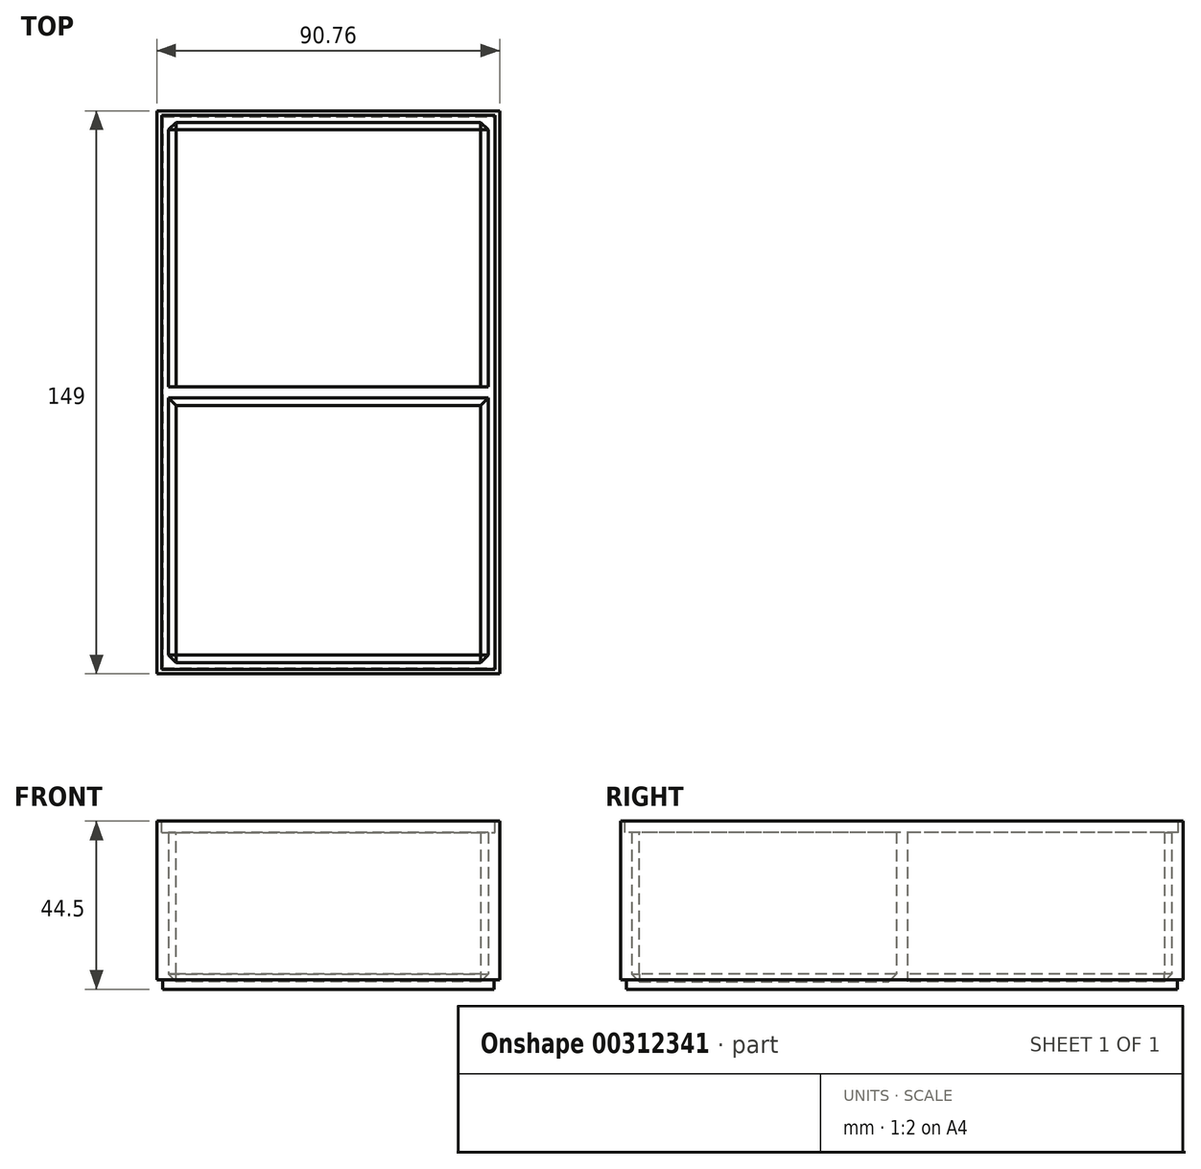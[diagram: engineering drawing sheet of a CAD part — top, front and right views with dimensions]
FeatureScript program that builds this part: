
annotation { "Feature Type Name" : "Feature", "Feature Type Description" : "" }
export const myFeature = defineFeature(function(context is Context, id is Id, definition is map)
    precondition{}
    {
        {
            assignVariable(context, id + "F0", {"name" : "BoxHeight", "anyValue" : 44.5 * mm});
        }
        {
            var Q0;
            Q0=qCreatedBy(makeId("Top.planeOp"),FACE);
            var sketch = newSketch(context, id + "F1", { "sketchPlane" : qUnion([Q0])});
            skLineSegment(sketch, "E0.bottom", {"start": v(-45.37, 74.5) * mm, "end": v(45.38, 74.5) * mm});
            skLineSegment(sketch, "E0.top", {"start": v(-45.38, -74.5) * mm, "end": v(45.37, -74.5) * mm});
            skLineSegment(sketch, "E0.left", {"start": v(-45.37, 74.5) * mm, "end": v(-45.38, -74.5) * mm});
            skLineSegment(sketch, "E0.right", {"start": v(45.38, 74.5) * mm, "end": v(45.37, -74.5) * mm});
            skPoint(sketch, "E0.middle", {"position": v(0, 0) * mm});
            skLineSegment(sketch, "E1.0", {"start": v(-42.37, 71.5) * mm, "end": v(42.38, 71.5) * mm});
            skLineSegment(sketch, "E1.1", {"start": v(-42.37, 71.5) * mm, "end": v(-42.38, -71.5) * mm});
            skLineSegment(sketch, "E1.2", {"start": v(-42.38, -71.5) * mm, "end": v(42.37, -71.5) * mm});
            skLineSegment(sketch, "E1.3", {"start": v(42.38, 71.5) * mm, "end": v(42.37, -71.5) * mm});
            skSolve(sketch);
        }
        {
            var Q0;
            Q0=makeQuery(id+"F1.imprint","IMPRINT",FACE,{"disambiguationData":[TD([[makeQuery(id+"F1.imprint","IMPRINT",EDGE,{"derivedFrom":sQuery(id+"F1.wireOp",EDGE,"E0.bottom")}),-1.0]])]});
            extrude(context, id + "F2", {"entities" : qUnion([Q0]), "depth" : getVariable(context, 'BoxHeight')});
        }
        {
            var Q0;
            Q0=qSketchRegion(id+"F1",true);
            var Q1;
            Q1=makeQuery(id+"F1.imprint","IMPRINT",FACE,{"disambiguationData":[TD([[makeQuery(id+"F1.imprint","IMPRINT",EDGE,{"derivedFrom":sQuery(id+"F1.wireOp",EDGE,"E1.0")}),-1.0]])]});
            extrude(context, id + "F3", {"entities" : qUnion([Q0, Q1]), "operationType" : NewBodyOperationType.ADD, "depth" : 2 * mm});
        }
        {
            var Q0;
            Q0=makeQuery(id+"F2.opExtrude","CAP_FACE",FACE,{"disambiguationData":[OSD([sQuery(id+"F1.wireOp",EDGE,"E0.bottom"),sQuery(id+"F1.wireOp",EDGE,"E0.top"),sQuery(id+"F1.wireOp",EDGE,"E0.left"),sQuery(id+"F1.wireOp",EDGE,"E0.right"),sQuery(id+"F1.wireOp",EDGE,"E1.0"),sQuery(id+"F1.wireOp",EDGE,"E1.1"),sQuery(id+"F1.wireOp",EDGE,"E1.2"),sQuery(id+"F1.wireOp",EDGE,"E1.3")])],"isStart":false});
            var sketch = newSketch(context, id + "F4", { "sketchPlane" : qUnion([Q0])});
            skLineSegment(sketch, "E2.0", {"start": v(-45.37, 74.5) * mm, "end": v(45.38, 74.5) * mm});
            skLineSegment(sketch, "E2.1", {"start": v(45.38, 74.5) * mm, "end": v(45.37, -74.5) * mm});
            skLineSegment(sketch, "E2.2", {"start": v(-45.37, 74.5) * mm, "end": v(-45.38, -74.5) * mm});
            skLineSegment(sketch, "E2.3", {"start": v(-45.38, -74.5) * mm, "end": v(45.37, -74.5) * mm});
            skLineSegment(sketch, "E3.0", {"start": v(-44.17, 73.3) * mm, "end": v(-44.18, -73.3) * mm});
            skLineSegment(sketch, "E3.1", {"start": v(-44.17, 73.3) * mm, "end": v(44.17, 73.3) * mm});
            skLineSegment(sketch, "E3.2", {"start": v(44.18, 73.3) * mm, "end": v(44.17, -73.3) * mm});
            skLineSegment(sketch, "E3.3", {"start": v(-44.18, -73.3) * mm, "end": v(44.17, -73.3) * mm});
            skSolve(sketch);
        }
        {
            var Q0;
            Q0=makeQuery(id+"F4.imprint","IMPRINT",FACE,{"disambiguationData":[TD([[makeQuery(id+"F4.imprint","IMPRINT",EDGE,{"derivedFrom":sQuery(id+"F4.wireOp",EDGE,"E3.0")}),1.0]])]});
            extrude(context, id + "F5", {"entities" : qUnion([Q0]), "operationType" : NewBodyOperationType.REMOVE, "oppositeDirection" : true, "depth" : 3 * mm});
        }
        {
            var Q0;
            {var subQ0=sQuery(id+"F1.wireOp",EDGE,"E0.right");var subQ1=sQuery(id+"F1.wireOp",EDGE,"E0.left");var subQ2=sQuery(id+"F1.wireOp",EDGE,"E0.top");var subQ3=sQuery(id+"F1.wireOp",EDGE,"E0.bottom");Q0=makeQuery(id+"F3.boolean.opBoolean","MERGE",FACE,{"derivedFrom":[makeQuery(id+"F2.opExtrude","CAP_FACE",FACE,{"disambiguationData":[OSD([subQ3,subQ2,subQ1,subQ0,sQuery(id+"F1.wireOp",EDGE,"E1.0"),sQuery(id+"F1.wireOp",EDGE,"E1.1"),sQuery(id+"F1.wireOp",EDGE,"E1.2"),sQuery(id+"F1.wireOp",EDGE,"E1.3")])],"isStart":true}),makeQuery(id+"F3.opExtrude","CAP_FACE",FACE,{"disambiguationData":[OSD([subQ3,subQ2,subQ1,subQ0])],"isStart":true})]});}
            var sketch = newSketch(context, id + "F6", { "sketchPlane" : qUnion([Q0])});
            skLineSegment(sketch, "E4.0", {"start": v(-45.37, -74.5) * mm, "end": v(-45.38, 74.5) * mm});
            skLineSegment(sketch, "E5.0", {"start": v(-45.38, 74.5) * mm, "end": v(45.37, 74.5) * mm});
            skLineSegment(sketch, "E6.0", {"start": v(45.38, -74.5) * mm, "end": v(45.37, 74.5) * mm});
            skLineSegment(sketch, "E7.0", {"start": v(-45.37, -74.5) * mm, "end": v(45.38, -74.5) * mm});
            skLineSegment(sketch, "E8.0", {"start": v(-43.87, -73) * mm, "end": v(-43.88, 73) * mm});
            skLineSegment(sketch, "E8.1", {"start": v(-43.87, -73) * mm, "end": v(43.88, -73) * mm});
            skLineSegment(sketch, "E8.2", {"start": v(43.88, -73) * mm, "end": v(43.87, 73) * mm});
            skLineSegment(sketch, "E8.3", {"start": v(-43.88, 73) * mm, "end": v(43.87, 73) * mm});
            skSolve(sketch);
        }
        {
            var Q0;
            Q0=makeQuery(id+"F6.imprint","IMPRINT",FACE,{"disambiguationData":[TD([[makeQuery(id+"F6.imprint","IMPRINT",EDGE,{"derivedFrom":sQuery(id+"F6.wireOp",EDGE,"E4.0")}),-1.0]])]});
            extrude(context, id + "F7", {"entities" : qUnion([Q0]), "operationType" : NewBodyOperationType.REMOVE, "oppositeDirection" : true, "depth" : 2.5 * mm});
        }
        {
            var Q0;
            Q0=makeQuery(id+"F2.opExtrude","SWEPT_FACE",FACE,{"disambiguationData":[OSD([sQuery(id+"F1.wireOp",EDGE,"E1.3")])]});
            var sketch = newSketch(context, id + "F8", { "sketchPlane" : qUnion([Q0])});
            skLineSegment(sketch, "E9", {"start": v(0, 41.5) * mm, "end": v(0, 2) * mm});
            skSolve(sketch);
        }
        {
            var Q0;
            Q0=sQuery(id+"F8.wireOp",EDGE,"E9");
            extrude(context, id + "F9", {"bodyType" : ToolBodyType.SURFACE, "surfaceEntities" : qUnion([Q0]), "endBound" : BoundingType.UP_TO_NEXT, "depth" : 25 * mm});
        }
        {
            var Q0;
            Q0=makeQuery(id+"F9.opExtrude","SWEPT_FACE",FACE,{"disambiguationData":[OSD([sQuery(id+"F8.wireOp",EDGE,"E9")])]});
            extrude(context, id + "F10", {"entities" : qUnion([Q0]), "operationType" : NewBodyOperationType.ADD, "endBound" : BoundingType.SYMMETRIC, "depth" : 3 * mm});
        }
        {
            var Q0;
            Q0=makeQuery(id+"F3.boolean.opBoolean","INTERSECT",EDGE,{"derivedFrom":[makeQuery(id+"F2.opExtrude","SWEPT_FACE",FACE,{"disambiguationData":[OSD([sQuery(id+"F1.wireOp",EDGE,"E1.0")])]}),makeQuery(id+"F3.opExtrude","CAP_FACE",FACE,{"disambiguationData":[OSD([sQuery(id+"F1.wireOp",EDGE,"E0.bottom"),sQuery(id+"F1.wireOp",EDGE,"E0.top"),sQuery(id+"F1.wireOp",EDGE,"E0.left"),sQuery(id+"F1.wireOp",EDGE,"E0.right")])],"isStart":false})]});
            var Q1;
            Q1=makeQuery(id+"F3.boolean.opBoolean","INTERSECT",EDGE,{"derivedFrom":[makeQuery(id+"F2.opExtrude","SWEPT_FACE",FACE,{"disambiguationData":[OSD([sQuery(id+"F1.wireOp",EDGE,"E1.3")])]}),makeQuery(id+"F3.opExtrude","CAP_FACE",FACE,{"disambiguationData":[OSD([sQuery(id+"F1.wireOp",EDGE,"E0.bottom"),sQuery(id+"F1.wireOp",EDGE,"E0.top"),sQuery(id+"F1.wireOp",EDGE,"E0.left"),sQuery(id+"F1.wireOp",EDGE,"E0.right")])],"isStart":false})]});
            var Q2;
            Q2=makeQuery(id+"F3.boolean.opBoolean","INTERSECT",EDGE,{"derivedFrom":[makeQuery(id+"F2.opExtrude","SWEPT_FACE",FACE,{"disambiguationData":[OSD([sQuery(id+"F1.wireOp",EDGE,"E1.1")])]}),makeQuery(id+"F3.opExtrude","CAP_FACE",FACE,{"disambiguationData":[OSD([sQuery(id+"F1.wireOp",EDGE,"E0.bottom"),sQuery(id+"F1.wireOp",EDGE,"E0.top"),sQuery(id+"F1.wireOp",EDGE,"E0.left"),sQuery(id+"F1.wireOp",EDGE,"E0.right")])],"isStart":false})]});
            var Q3;
            Q3=makeQuery(id+"F3.boolean.opBoolean","INTERSECT",EDGE,{"derivedFrom":[makeQuery(id+"F2.opExtrude","SWEPT_FACE",FACE,{"disambiguationData":[OSD([sQuery(id+"F1.wireOp",EDGE,"E1.2")])]}),makeQuery(id+"F3.opExtrude","CAP_FACE",FACE,{"disambiguationData":[OSD([sQuery(id+"F1.wireOp",EDGE,"E0.bottom"),sQuery(id+"F1.wireOp",EDGE,"E0.top"),sQuery(id+"F1.wireOp",EDGE,"E0.left"),sQuery(id+"F1.wireOp",EDGE,"E0.right")])],"isStart":false})]});
            var Q4;
            Q4=makeQuery(id+"F2.opExtrude","SWEPT_EDGE",EDGE,{"disambiguationData":[OSD([sQuery(id+"F1.wireOp",EDGE,"E1.2"),sQuery(id+"F1.wireOp",EDGE,"E1.3")])]});
            var Q5;
            Q5=makeQuery(id+"F2.opExtrude","SWEPT_EDGE",EDGE,{"disambiguationData":[OSD([sQuery(id+"F1.wireOp",EDGE,"E1.0"),sQuery(id+"F1.wireOp",EDGE,"E1.3")])]});
            var Q6;
            Q6=makeQuery(id+"F2.opExtrude","SWEPT_EDGE",EDGE,{"disambiguationData":[OSD([sQuery(id+"F1.wireOp",EDGE,"E1.0"),sQuery(id+"F1.wireOp",EDGE,"E1.1")])]});
            var Q7;
            Q7=makeQuery(id+"F2.opExtrude","SWEPT_EDGE",EDGE,{"disambiguationData":[OSD([sQuery(id+"F1.wireOp",EDGE,"E1.1"),sQuery(id+"F1.wireOp",EDGE,"E1.2")])]});
            var Q8;
            Q8=makeQuery(id+"F10.opExtrude","CAP_EDGE",EDGE,{"disambiguationData":[OSD([sQuery(id+"F1.wireOp",EDGE,"E0.bottom"),sQuery(id+"F1.wireOp",EDGE,"E0.top"),sQuery(id+"F1.wireOp",EDGE,"E0.left"),sQuery(id+"F1.wireOp",EDGE,"E0.right")])],"isStart":false});
            var Q9;
            Q9=makeQuery(id+"F10.boolean.opBoolean","SPLIT",FACE,{"disambiguationData":[TD([makeQuery(id+"F2.opExtrude","SWEPT_FACE",FACE,{"disambiguationData":[OSD([sQuery(id+"F1.wireOp",EDGE,"E1.2")])]})])],"derivedFrom":makeQuery(id+"F3.opExtrude","CAP_FACE",FACE,{"disambiguationData":[OSD([sQuery(id+"F1.wireOp",EDGE,"E0.bottom"),sQuery(id+"F1.wireOp",EDGE,"E0.top"),sQuery(id+"F1.wireOp",EDGE,"E0.left"),sQuery(id+"F1.wireOp",EDGE,"E0.right")])],"isStart":false})});
            chamfer(context, id + "F11", {"entities" : qUnion([Q0, Q1, Q2, Q3, Q4, Q5, Q6, Q7, Q8, Q9]), "width" : 2 * mm, "tangentPropagation" : true});
        }
    });
